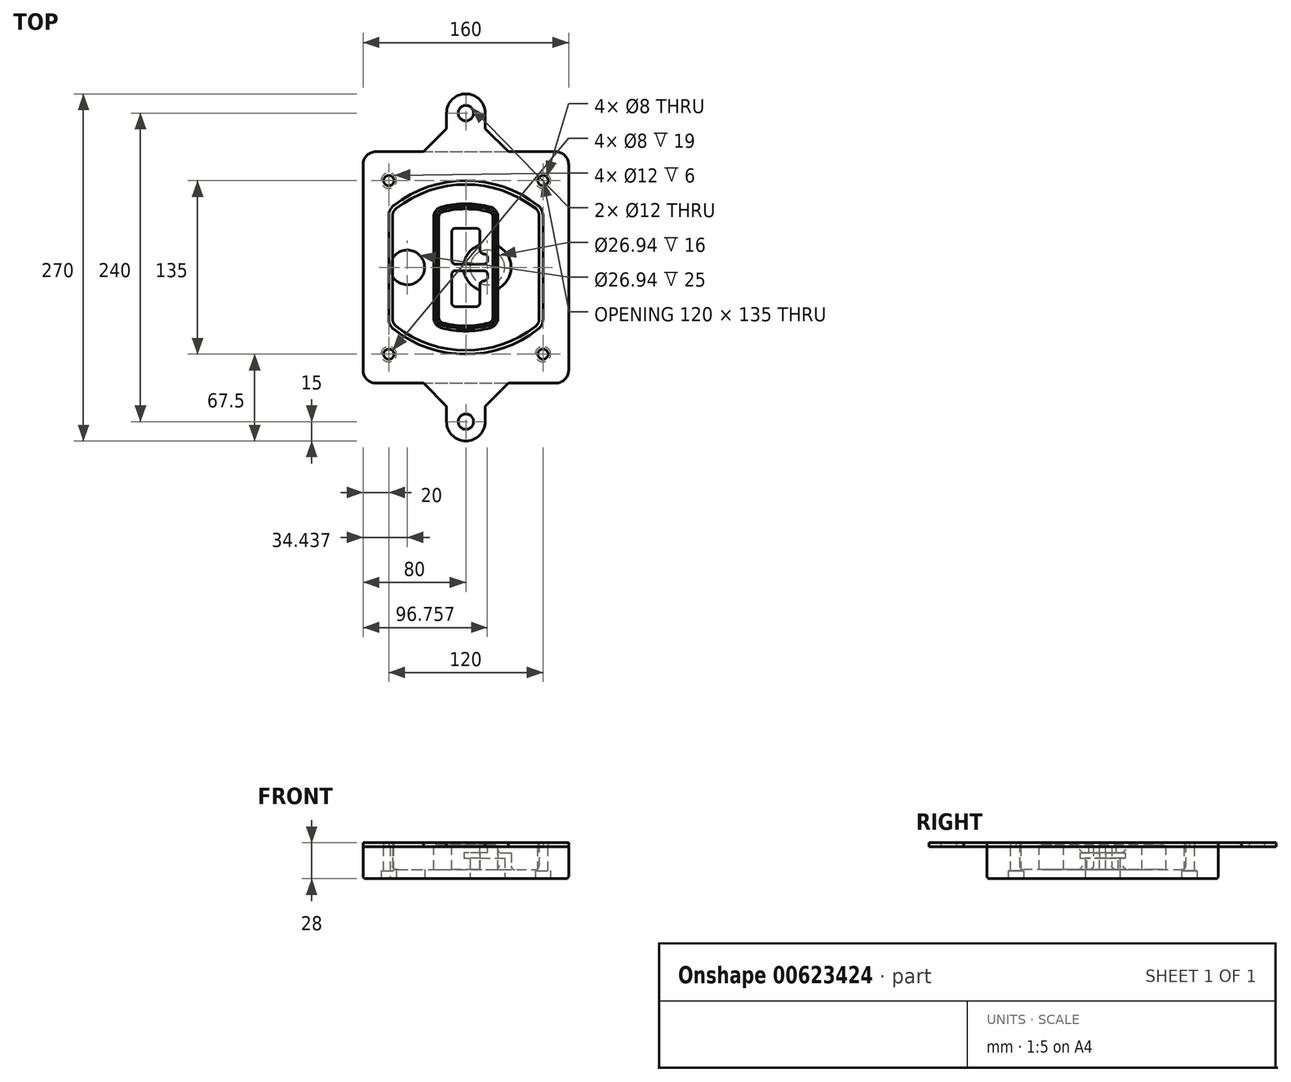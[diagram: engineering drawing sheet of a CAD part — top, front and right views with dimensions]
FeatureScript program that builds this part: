
annotation { "Feature Type Name" : "Feature", "Feature Type Description" : "" }
export const myFeature = defineFeature(function(context is Context, id is Id, definition is map)
    precondition{}
    {
        {
            var Q0;
            Q0=qCreatedBy(makeId("Top.planeOp"),FACE);
            var sketch = newSketch(context, id + "F0", { "sketchPlane" : qUnion([Q0])});
            skPoint(sketch, "E0.rect.middle", {"position": v(0, 0) * mm});
            skLineSegment(sketch, "E1.bottom", {"start": v(-70, -90) * mm, "end": v(70, -90) * mm});
            skLineSegment(sketch, "E1.top", {"start": v(-70, 90) * mm, "end": v(70, 90) * mm});
            skLineSegment(sketch, "E1.left", {"start": v(-80, -80) * mm, "end": v(-80, 80) * mm});
            skLineSegment(sketch, "E1.right", {"start": v(80, -80) * mm, "end": v(80, 80) * mm});
            skLineSegment(sketch, "E2", {"start": v(-80, 90) * mm, "end": v(80, -90) * mm, "construction": true});
            skLineSegment(sketch, "E3", {"start": v(80, 90) * mm, "end": v(-80, -90) * mm, "construction": true});
            skCircle(sketch, "E4", {"center": v(-60, 67.5) * mm, "radius": 4 * mm});
            skCircle(sketch, "E5", {"center": v(60, 67.5) * mm, "radius": 4 * mm});
            skCircle(sketch, "E6", {"center": v(60, -67.5) * mm, "radius": 4 * mm});
            skCircle(sketch, "E7", {"center": v(-60, -67.5) * mm, "radius": 4 * mm});
            skLineSegment(sketch, "E8", {"start": v(-60, 67.5) * mm, "end": v(60, 67.5) * mm, "construction": true});
            skLineSegment(sketch, "E9", {"start": v(60, 67.5) * mm, "end": v(60, -67.5) * mm, "construction": true});
            skLineSegment(sketch, "E10", {"start": v(60, -67.5) * mm, "end": v(-60, -67.5) * mm, "construction": true});
            skLineSegment(sketch, "E11", {"start": v(-60, -67.5) * mm, "end": v(-60, 67.5) * mm, "construction": true});
            skLineSegment(sketch, "E12", {"start": v(-60, 40.3) * mm, "end": v(-60, -40.3) * mm});
            skLineSegment(sketch, "E13", {"start": v(60, 40.3) * mm, "end": v(60, -40.3) * mm});
            skArc(sketch, "E14", {"start": v(56.15, 48.18) * mm, "mid": v(0, 67.5) * mm, "end": v(-56.15, 48.18) * mm});
            skArc(sketch, "E15", {"start": v(-56.15, -48.18) * mm, "mid": v(0, -67.5) * mm, "end": v(56.15, -48.18) * mm});
            skLineSegment(sketch, "E16", {"start": v(-60, 0) * mm, "end": v(60, 0) * mm, "construction": true});
            skPoint(sketch, "E17.visualSharp", {"position": v(-60, -45) * mm});
            skArc(sketch, "E17.filletArc", {"start": v(-60, -40.3) * mm, "mid": v(-58.99, -44.68) * mm, "end": v(-56.15, -48.18) * mm});
            skPoint(sketch, "E18.visualSharp", {"position": v(-60, 45) * mm});
            skArc(sketch, "E18.filletArc", {"start": v(-56.15, 48.18) * mm, "mid": v(-58.99, 44.68) * mm, "end": v(-60, 40.3) * mm});
            skPoint(sketch, "E19.visualSharp", {"position": v(60, 45) * mm});
            skArc(sketch, "E19.filletArc", {"start": v(60, 40.3) * mm, "mid": v(58.99, 44.68) * mm, "end": v(56.15, 48.18) * mm});
            skPoint(sketch, "E20.visualSharp", {"position": v(60, -45) * mm});
            skArc(sketch, "E20.filletArc", {"start": v(56.15, -48.18) * mm, "mid": v(58.99, -44.68) * mm, "end": v(60, -40.3) * mm});
            skPoint(sketch, "E21.visualSharp", {"position": v(-80, 90) * mm});
            skArc(sketch, "E21.filletArc", {"start": v(-70, 90) * mm, "mid": v(-77.07, 87.07) * mm, "end": v(-80, 80) * mm});
            skPoint(sketch, "E22.visualSharp", {"position": v(80, 90) * mm});
            skArc(sketch, "E22.filletArc", {"start": v(80, 80) * mm, "mid": v(77.07, 87.07) * mm, "end": v(70, 90) * mm});
            skPoint(sketch, "E23.visualSharp", {"position": v(80, -90) * mm});
            skArc(sketch, "E23.filletArc", {"start": v(70, -90) * mm, "mid": v(77.07, -87.07) * mm, "end": v(80, -80) * mm});
            skPoint(sketch, "E24.visualSharp", {"position": v(-80, -90) * mm});
            skArc(sketch, "E24.filletArc", {"start": v(-80, -80) * mm, "mid": v(-77.07, -87.07) * mm, "end": v(-70, -90) * mm});
            skArc(sketch, "E25.0", {"start": v(57, 40.3) * mm, "mid": v(56.3, 43.36) * mm, "end": v(54.3, 45.81) * mm});
            skLineSegment(sketch, "E25.1", {"start": v(57, 40.3) * mm, "end": v(57, -40.3) * mm});
            skArc(sketch, "E25.2", {"start": v(54.3, -45.81) * mm, "mid": v(56.3, -43.36) * mm, "end": v(57, -40.3) * mm});
            skArc(sketch, "E25.3", {"start": v(-54.3, -45.81) * mm, "mid": v(0, -64.5) * mm, "end": v(54.3, -45.81) * mm});
            skArc(sketch, "E25.4", {"start": v(-57, -40.3) * mm, "mid": v(-56.3, -43.36) * mm, "end": v(-54.3, -45.81) * mm});
            skArc(sketch, "E25.5", {"start": v(54.3, 45.81) * mm, "mid": v(0, 64.5) * mm, "end": v(-54.3, 45.81) * mm});
            skLineSegment(sketch, "E25.6", {"start": v(-57, 40.3) * mm, "end": v(-57, -40.3) * mm});
            skArc(sketch, "E25.7", {"start": v(-54.3, 45.81) * mm, "mid": v(-56.3, 43.36) * mm, "end": v(-57, 40.3) * mm});
            skArc(sketch, "E26.0", {"start": v(-58.62, 51.33) * mm, "mid": v(-62.58, 46.43) * mm, "end": v(-64, 40.3) * mm});
            skArc(sketch, "E26.1", {"start": v(58.62, 51.33) * mm, "mid": v(0, 71.5) * mm, "end": v(-58.62, 51.33) * mm});
            skArc(sketch, "E26.2", {"start": v(64, 40.3) * mm, "mid": v(62.58, 46.43) * mm, "end": v(58.62, 51.33) * mm});
            skLineSegment(sketch, "E26.3", {"start": v(64, 40.3) * mm, "end": v(64, -40.3) * mm});
            skArc(sketch, "E26.4", {"start": v(58.62, -51.33) * mm, "mid": v(62.58, -46.43) * mm, "end": v(64, -40.3) * mm});
            skLineSegment(sketch, "E26.5", {"start": v(-64, 40.3) * mm, "end": v(-64, -40.3) * mm});
            skArc(sketch, "E26.6", {"start": v(-58.62, -51.33) * mm, "mid": v(0, -71.5) * mm, "end": v(58.62, -51.33) * mm});
            skArc(sketch, "E26.7", {"start": v(-64, -40.3) * mm, "mid": v(-62.58, -46.43) * mm, "end": v(-58.62, -51.33) * mm});
            skSolve(sketch);
        }
        {
            var Q0;
            Q0=makeQuery(id+"F0.imprint","IMPRINT",FACE,{"disambiguationData":[TD([[makeQuery(id+"F0.imprint","IMPRINT",EDGE,{"derivedFrom":sQuery(id+"F0.wireOp",EDGE,"E1.bottom")}),1.0]])]});
            var Q1;
            Q1=makeQuery(id+"F0.imprint","IMPRINT",FACE,{"disambiguationData":[TD([[makeQuery(id+"F0.imprint","IMPRINT",EDGE,{"derivedFrom":sQuery(id+"F0.wireOp",EDGE,"E12")}),1.0]])]});
            var Q2;
            Q2=makeQuery(id+"F0.imprint","IMPRINT",FACE,{"disambiguationData":[TD([[makeQuery(id+"F0.imprint","IMPRINT",EDGE,{"derivedFrom":sQuery(id+"F0.wireOp",EDGE,"E25.0")}),1.0]])]});
            var Q3;
            Q3=makeQuery(id+"F0.imprint","IMPRINT",FACE,{"disambiguationData":[TD([[makeQuery(id+"F0.imprint","IMPRINT",EDGE,{"derivedFrom":sQuery(id+"F0.wireOp",EDGE,"E12")}),-1.0]])]});
            extrude(context, id + "F1", {"entities" : qUnion([Q0, Q1, Q2, Q3]), "oppositeDirection" : true, "depth" : 25 * mm});
        }
        {
            var Q0;
            Q0=makeQuery(id+"F0.imprint","IMPRINT",FACE,{"disambiguationData":[TD([[makeQuery(id+"F0.imprint","IMPRINT",EDGE,{"derivedFrom":sQuery(id+"F0.wireOp",EDGE,"E12")}),1.0]])]});
            extrude(context, id + "F2", {"entities" : qUnion([Q0]), "operationType" : NewBodyOperationType.ADD, "depth" : 3 * mm});
        }
        {
            var Q0;
            Q0=makeQuery(id+"F0.imprint","IMPRINT",FACE,{"disambiguationData":[TD([[makeQuery(id+"F0.imprint","IMPRINT",EDGE,{"derivedFrom":sQuery(id+"F0.wireOp",EDGE,"E25.0")}),1.0]])]});
            extrude(context, id + "F3", {"entities" : qUnion([Q0]), "operationType" : NewBodyOperationType.REMOVE, "oppositeDirection" : true, "depth" : 18 * mm});
        }
        {
            var Q0;
            Q0=makeQuery(id+"F2.opExtrude","CAP_FACE",FACE,{"disambiguationData":[OSD([sQuery(id+"F0.wireOp",EDGE,"E12"),sQuery(id+"F0.wireOp",EDGE,"E13"),sQuery(id+"F0.wireOp",EDGE,"E14"),sQuery(id+"F0.wireOp",EDGE,"E15"),sQuery(id+"F0.wireOp",EDGE,"E17.filletArc"),sQuery(id+"F0.wireOp",EDGE,"E18.filletArc"),sQuery(id+"F0.wireOp",EDGE,"E19.filletArc"),sQuery(id+"F0.wireOp",EDGE,"E20.filletArc"),sQuery(id+"F0.wireOp",EDGE,"E25.0"),sQuery(id+"F0.wireOp",EDGE,"E25.1"),sQuery(id+"F0.wireOp",EDGE,"E25.2"),sQuery(id+"F0.wireOp",EDGE,"E25.3"),sQuery(id+"F0.wireOp",EDGE,"E25.4"),sQuery(id+"F0.wireOp",EDGE,"E25.5"),sQuery(id+"F0.wireOp",EDGE,"E25.6"),sQuery(id+"F0.wireOp",EDGE,"E25.7")])],"isStart":false});
            var sketch = newSketch(context, id + "F4", { "sketchPlane" : qUnion([Q0])});
            skArc(sketch, "E27.0", {"start": v(-19.08, -46.97) * mm, "mid": v(0, -49.5) * mm, "end": v(19.08, -46.97) * mm});
            skArc(sketch, "E28.0", {"start": v(19.08, 46.97) * mm, "mid": v(0, 49.5) * mm, "end": v(-19.08, 46.97) * mm});
            skLineSegment(sketch, "E29", {"start": v(-25, 39.25) * mm, "end": v(-25, -39.25) * mm});
            skLineSegment(sketch, "E30", {"start": v(25, 39.25) * mm, "end": v(25, -39.25) * mm});
            skLineSegment(sketch, "E31", {"start": v(-25, 45.1) * mm, "end": v(25, 45.1) * mm, "construction": true});
            skLineSegment(sketch, "E32", {"start": v(-25, -45.1) * mm, "end": v(25, -45.1) * mm, "construction": true});
            skPoint(sketch, "E33.visualSharp", {"position": v(-25, 45.1) * mm});
            skArc(sketch, "E33.filletArc", {"start": v(-19.08, 46.97) * mm, "mid": v(-23.35, 44.11) * mm, "end": v(-25, 39.25) * mm});
            skPoint(sketch, "E34.visualSharp", {"position": v(25, 45.1) * mm});
            skArc(sketch, "E34.filletArc", {"start": v(25, 39.25) * mm, "mid": v(23.35, 44.11) * mm, "end": v(19.08, 46.97) * mm});
            skPoint(sketch, "E35.visualSharp", {"position": v(25, -45.1) * mm});
            skArc(sketch, "E35.filletArc", {"start": v(19.08, -46.97) * mm, "mid": v(23.35, -44.11) * mm, "end": v(25, -39.25) * mm});
            skPoint(sketch, "E36.visualSharp", {"position": v(-25, -45.1) * mm});
            skArc(sketch, "E36.filletArc", {"start": v(-25, -39.25) * mm, "mid": v(-23.35, -44.11) * mm, "end": v(-19.08, -46.97) * mm});
            skArc(sketch, "E37.0", {"start": v(54.3, 45.81) * mm, "mid": v(0, 64.5) * mm, "end": v(-54.3, 45.81) * mm});
            skArc(sketch, "E37.1", {"start": v(-54.3, 45.81) * mm, "mid": v(-56.3, 43.36) * mm, "end": v(-57, 40.3) * mm});
            skLineSegment(sketch, "E37.2", {"start": v(-57, 40.3) * mm, "end": v(-57, -40.3) * mm});
            skArc(sketch, "E37.3", {"start": v(-57, -40.3) * mm, "mid": v(-56.3, -43.36) * mm, "end": v(-54.3, -45.81) * mm});
            skArc(sketch, "E37.4", {"start": v(-54.3, -45.81) * mm, "mid": v(0, -64.5) * mm, "end": v(54.3, -45.81) * mm});
            skArc(sketch, "E37.5", {"start": v(54.3, -45.81) * mm, "mid": v(56.3, -43.36) * mm, "end": v(57, -40.3) * mm});
            skLineSegment(sketch, "E37.6", {"start": v(57, 40.3) * mm, "end": v(57, -40.3) * mm});
            skArc(sketch, "E37.7", {"start": v(57, 40.3) * mm, "mid": v(56.3, 43.36) * mm, "end": v(54.3, 45.81) * mm});
            skLineSegment(sketch, "E38.0", {"start": v(23, 39.25) * mm, "end": v(23, -39.25) * mm});
            skArc(sketch, "E38.1", {"start": v(18.56, -45.04) * mm, "mid": v(21.76, -42.9) * mm, "end": v(23, -39.25) * mm});
            skArc(sketch, "E38.2", {"start": v(-18.56, -45.04) * mm, "mid": v(0, -47.5) * mm, "end": v(18.56, -45.04) * mm});
            skArc(sketch, "E38.3", {"start": v(-23, -39.25) * mm, "mid": v(-21.76, -42.9) * mm, "end": v(-18.56, -45.04) * mm});
            skLineSegment(sketch, "E38.4", {"start": v(-23, 39.25) * mm, "end": v(-23, -39.25) * mm});
            skArc(sketch, "E38.5", {"start": v(23, 39.25) * mm, "mid": v(21.76, 42.9) * mm, "end": v(18.56, 45.04) * mm});
            skArc(sketch, "E38.6", {"start": v(-18.56, 45.04) * mm, "mid": v(-21.76, 42.9) * mm, "end": v(-23, 39.25) * mm});
            skArc(sketch, "E38.7", {"start": v(18.56, 45.04) * mm, "mid": v(0, 47.5) * mm, "end": v(-18.56, 45.04) * mm});
            skArc(sketch, "E39.0", {"start": v(21, 39.25) * mm, "mid": v(20.18, 41.68) * mm, "end": v(18.04, 43.1) * mm});
            skLineSegment(sketch, "E39.1", {"start": v(21, 39.25) * mm, "end": v(21, -39.25) * mm});
            skArc(sketch, "E39.2", {"start": v(18.04, -43.1) * mm, "mid": v(20.18, -41.68) * mm, "end": v(21, -39.25) * mm});
            skArc(sketch, "E39.3", {"start": v(-18.04, -43.1) * mm, "mid": v(0, -45.5) * mm, "end": v(18.04, -43.1) * mm});
            skArc(sketch, "E39.4", {"start": v(-21, -39.25) * mm, "mid": v(-20.18, -41.68) * mm, "end": v(-18.04, -43.1) * mm});
            skArc(sketch, "E39.5", {"start": v(18.04, 43.1) * mm, "mid": v(0, 45.5) * mm, "end": v(-18.04, 43.1) * mm});
            skLineSegment(sketch, "E39.6", {"start": v(-21, 39.25) * mm, "end": v(-21, -39.25) * mm});
            skArc(sketch, "E39.7", {"start": v(-18.04, 43.1) * mm, "mid": v(-20.18, 41.68) * mm, "end": v(-21, 39.25) * mm});
            skLineSegment(sketch, "E40", {"start": v(-25, 0) * mm, "end": v(25, 0) * mm, "construction": true});
            skLineSegment(sketch, "E41", {"start": v(-11, 5.5) * mm, "end": v(-11, 27.5) * mm});
            skLineSegment(sketch, "E42", {"start": v(-8, 30.5) * mm, "end": v(8, 30.5) * mm});
            skLineSegment(sketch, "E43", {"start": v(11, 27.5) * mm, "end": v(11, 13.5) * mm});
            skLineSegment(sketch, "E44", {"start": v(14, 10.5) * mm, "end": v(14, 10.5) * mm});
            skLineSegment(sketch, "E45", {"start": v(17, 7.5) * mm, "end": v(17, 5.5) * mm});
            skLineSegment(sketch, "E46", {"start": v(14, 2.5) * mm, "end": v(-8, 2.5) * mm});
            skPoint(sketch, "E47.visualSharp", {"position": v(-11, 30.5) * mm});
            skArc(sketch, "E47.filletArc", {"start": v(-8, 30.5) * mm, "mid": v(-10.12, 29.62) * mm, "end": v(-11, 27.5) * mm});
            skPoint(sketch, "E48.visualSharp", {"position": v(11, 30.5) * mm});
            skArc(sketch, "E48.filletArc", {"start": v(11, 27.5) * mm, "mid": v(10.12, 29.62) * mm, "end": v(8, 30.5) * mm});
            skPoint(sketch, "E49.visualSharp", {"position": v(11, 10.5) * mm});
            skArc(sketch, "E49.filletArc", {"start": v(11, 13.5) * mm, "mid": v(11.88, 11.38) * mm, "end": v(14, 10.5) * mm});
            skPoint(sketch, "E50.visualSharp", {"position": v(17, 10.5) * mm});
            skArc(sketch, "E50.filletArc", {"start": v(17, 7.5) * mm, "mid": v(16.12, 9.62) * mm, "end": v(14, 10.5) * mm});
            skPoint(sketch, "E51.visualSharp", {"position": v(17, 2.5) * mm});
            skArc(sketch, "E51.filletArc", {"start": v(14, 2.5) * mm, "mid": v(16.12, 3.38) * mm, "end": v(17, 5.5) * mm});
            skPoint(sketch, "E52.visualSharp", {"position": v(-11, 2.5) * mm});
            skArc(sketch, "E52.filletArc", {"start": v(-11, 5.5) * mm, "mid": v(-10.12, 3.38) * mm, "end": v(-8, 2.5) * mm});
            skLineSegment(sketch, "E53.0.MirrorCS", {"start": v(14, -2.5) * mm, "end": v(-8, -2.5) * mm});
            skArc(sketch, "E54.0.MirrorCS", {"start": v(-11, -5.5) * mm, "mid": v(-10.12, -3.38) * mm, "end": v(-8, -2.5) * mm});
            skLineSegment(sketch, "E55.0.MirrorCS", {"start": v(-11, -5.5) * mm, "end": v(-11, -27.5) * mm});
            skArc(sketch, "E56.0.MirrorCS", {"start": v(-8, -30.5) * mm, "mid": v(-10.12, -29.62) * mm, "end": v(-11, -27.5) * mm});
            skLineSegment(sketch, "E57.0.MirrorCS", {"start": v(-8, -30.5) * mm, "end": v(8, -30.5) * mm});
            skArc(sketch, "E58.0.MirrorCS", {"start": v(11, -27.5) * mm, "mid": v(10.12, -29.62) * mm, "end": v(8, -30.5) * mm});
            skLineSegment(sketch, "E59.0.MirrorCS", {"start": v(11, -27.5) * mm, "end": v(11, -13.5) * mm});
            skArc(sketch, "E60.0.MirrorCS", {"start": v(11, -13.5) * mm, "mid": v(11.88, -11.38) * mm, "end": v(14, -10.5) * mm});
            skArc(sketch, "E61.0.MirrorCS", {"start": v(17, -7.5) * mm, "mid": v(16.12, -9.62) * mm, "end": v(14, -10.5) * mm});
            skLineSegment(sketch, "E62.0.MirrorCS", {"start": v(17, -7.5) * mm, "end": v(17, -5.5) * mm});
            skArc(sketch, "E63.0.MirrorCS", {"start": v(14, -2.5) * mm, "mid": v(16.12, -3.38) * mm, "end": v(17, -5.5) * mm});
            skSolve(sketch);
        }
        {
            var Q0;
            Q0=makeQuery(id+"F4.imprint","IMPRINT",FACE,{"disambiguationData":[TD([[makeQuery(id+"F4.imprint","IMPRINT",EDGE,{"derivedFrom":sQuery(id+"F4.wireOp",EDGE,"E27.0")}),1.0]])]});
            var Q1;
            Q1=makeQuery(id+"F4.imprint","IMPRINT",FACE,{"disambiguationData":[TD([[makeQuery(id+"F4.imprint","IMPRINT",EDGE,{"derivedFrom":sQuery(id+"F4.wireOp",EDGE,"E38.0")}),-1.0]])]});
            var Q2;
            Q2=makeQuery(id+"F4.imprint","IMPRINT",FACE,{"disambiguationData":[TD([[makeQuery(id+"F4.imprint","IMPRINT",EDGE,{"derivedFrom":sQuery(id+"F4.wireOp",EDGE,"E39.0")}),1.0]])]});
            extrude(context, id + "F5", {"entities" : qUnion([Q0, Q1, Q2]), "operationType" : NewBodyOperationType.ADD, "endBound" : BoundingType.UP_TO_NEXT, "oppositeDirection" : true, "depth" : 25 * mm});
        }
        {
            var Q0;
            Q0=makeQuery(id+"F4.imprint","IMPRINT",FACE,{"disambiguationData":[TD([[makeQuery(id+"F4.imprint","IMPRINT",EDGE,{"derivedFrom":sQuery(id+"F4.wireOp",EDGE,"E38.0")}),-1.0]])]});
            extrude(context, id + "F6", {"entities" : qUnion([Q0]), "operationType" : NewBodyOperationType.REMOVE, "oppositeDirection" : true, "depth" : 2 * mm});
        }
        {
            var Q0;
            Q0=makeQuery(id+"F1.opExtrude","CAP_FACE",FACE,{"disambiguationData":[OSD([sQuery(id+"F0.wireOp",EDGE,"E1.bottom"),sQuery(id+"F0.wireOp",EDGE,"E1.top"),sQuery(id+"F0.wireOp",EDGE,"E1.left"),sQuery(id+"F0.wireOp",EDGE,"E1.right"),sQuery(id+"F0.wireOp",EDGE,"E4"),sQuery(id+"F0.wireOp",EDGE,"E5"),sQuery(id+"F0.wireOp",EDGE,"E6"),sQuery(id+"F0.wireOp",EDGE,"E7"),sQuery(id+"F0.wireOp",EDGE,"E21.filletArc"),sQuery(id+"F0.wireOp",EDGE,"E22.filletArc"),sQuery(id+"F0.wireOp",EDGE,"E23.filletArc"),sQuery(id+"F0.wireOp",EDGE,"E24.filletArc")])],"isStart":false});
            var sketch = newSketch(context, id + "F7", { "sketchPlane" : qUnion([Q0])});
            skCircle(sketch, "E64", {"center": v(16.76, 0) * mm, "radius": 13.47 * mm});
            skCircle(sketch, "E65", {"center": v(-45.56, 0) * mm, "radius": 13.47 * mm});
            skLineSegment(sketch, "E66", {"start": v(80, 0) * mm, "end": v(-80, 0) * mm});
            skCircle(sketch, "E67", {"center": v(16.76, 0) * mm, "radius": 18.47 * mm});
            skCircle(sketch, "E68", {"center": v(60, -67.5) * mm, "radius": 6 * mm});
            skCircle(sketch, "E69", {"center": v(-60, -67.5) * mm, "radius": 6 * mm});
            skCircle(sketch, "E70", {"center": v(-60, 67.5) * mm, "radius": 6 * mm});
            skCircle(sketch, "E71", {"center": v(60, 67.5) * mm, "radius": 6 * mm});
            skSolve(sketch);
        }
        {
            var Q0;
            {var subQ1=sQuery(id+"F7.wireOp",EDGE,"E66");var subQ4=sQuery(id+"F7.wireOp",EDGE,"E64");var subQ6=makeQuery(id+"F7.imprint","INTERSECT",VERTEX,{"disambiguationData":[OD(0.0)],"derivedFrom":[subQ4,subQ1]});Q0=makeQuery(id+"F7.imprint","IMPRINT",FACE,{"disambiguationData":[TD([[makeQuery(id+"F7.imprint","IMPRINT",EDGE,{"disambiguationData":[TD([[subQ6,-1.0]])],"derivedFrom":subQ4}),-1.0]])]});}
            var Q1;
            {var subQ0=sQuery(id+"F7.wireOp",EDGE,"E66");var subQ1=sQuery(id+"F7.wireOp",EDGE,"E64");var subQ3=makeQuery(id+"F7.imprint","INTERSECT",VERTEX,{"disambiguationData":[OD(0.0)],"derivedFrom":[subQ1,subQ0]});Q1=makeQuery(id+"F7.imprint","IMPRINT",FACE,{"disambiguationData":[TD([[makeQuery(id+"F7.imprint","IMPRINT",EDGE,{"disambiguationData":[TD([[subQ3,-1.0]])],"derivedFrom":subQ1}),1.0]])]});}
            var Q2;
            {var subQ0=sQuery(id+"F7.wireOp",EDGE,"E66");var subQ1=sQuery(id+"F7.wireOp",EDGE,"E64");var subQ3=makeQuery(id+"F7.imprint","INTERSECT",VERTEX,{"disambiguationData":[OD(0.0)],"derivedFrom":[subQ1,subQ0]});Q2=makeQuery(id+"F7.imprint","IMPRINT",FACE,{"disambiguationData":[TD([[makeQuery(id+"F7.imprint","IMPRINT",EDGE,{"disambiguationData":[TD([[subQ3,1.0]])],"derivedFrom":subQ1}),1.0]])]});}
            var Q3;
            {var subQ1=sQuery(id+"F7.wireOp",EDGE,"E66");var subQ4=sQuery(id+"F7.wireOp",EDGE,"E64");var subQ6=makeQuery(id+"F7.imprint","INTERSECT",VERTEX,{"disambiguationData":[OD(0.0)],"derivedFrom":[subQ4,subQ1]});Q3=makeQuery(id+"F7.imprint","IMPRINT",FACE,{"disambiguationData":[TD([[makeQuery(id+"F7.imprint","IMPRINT",EDGE,{"disambiguationData":[TD([[subQ6,1.0]])],"derivedFrom":subQ4}),-1.0]])]});}
            extrude(context, id + "F8", {"entities" : qUnion([Q0, Q1, Q2, Q3]), "operationType" : NewBodyOperationType.ADD, "oppositeDirection" : true, "depth" : 20 * mm});
        }
        {
            var Q0;
            {var subQ0=sQuery(id+"F7.wireOp",EDGE,"E66");var subQ1=sQuery(id+"F7.wireOp",EDGE,"E64");var subQ3=makeQuery(id+"F7.imprint","INTERSECT",VERTEX,{"disambiguationData":[OD(0.0)],"derivedFrom":[subQ1,subQ0]});Q0=makeQuery(id+"F7.imprint","IMPRINT",FACE,{"disambiguationData":[TD([[makeQuery(id+"F7.imprint","IMPRINT",EDGE,{"disambiguationData":[TD([[subQ3,-1.0]])],"derivedFrom":subQ1}),1.0]])]});}
            var Q1;
            {var subQ0=sQuery(id+"F7.wireOp",EDGE,"E66");var subQ1=sQuery(id+"F7.wireOp",EDGE,"E64");var subQ3=makeQuery(id+"F7.imprint","INTERSECT",VERTEX,{"disambiguationData":[OD(0.0)],"derivedFrom":[subQ1,subQ0]});Q1=makeQuery(id+"F7.imprint","IMPRINT",FACE,{"disambiguationData":[TD([[makeQuery(id+"F7.imprint","IMPRINT",EDGE,{"disambiguationData":[TD([[subQ3,1.0]])],"derivedFrom":subQ1}),1.0]])]});}
            extrude(context, id + "F9", {"entities" : qUnion([Q0, Q1]), "operationType" : NewBodyOperationType.REMOVE, "oppositeDirection" : true, "depth" : 16 * mm});
        }
        {
            var Q0;
            {var subQ0=sQuery(id+"F7.wireOp",EDGE,"E66");var subQ1=sQuery(id+"F7.wireOp",EDGE,"E65");var subQ3=makeQuery(id+"F7.imprint","INTERSECT",VERTEX,{"disambiguationData":[OD(0.0)],"derivedFrom":[subQ1,subQ0]});Q0=makeQuery(id+"F7.imprint","IMPRINT",FACE,{"disambiguationData":[TD([[makeQuery(id+"F7.imprint","IMPRINT",EDGE,{"disambiguationData":[TD([[subQ3,-1.0]])],"derivedFrom":subQ1}),1.0]])]});}
            var Q1;
            {var subQ0=sQuery(id+"F7.wireOp",EDGE,"E66");var subQ1=sQuery(id+"F7.wireOp",EDGE,"E65");var subQ3=makeQuery(id+"F7.imprint","INTERSECT",VERTEX,{"disambiguationData":[OD(0.0)],"derivedFrom":[subQ1,subQ0]});Q1=makeQuery(id+"F7.imprint","IMPRINT",FACE,{"disambiguationData":[TD([[makeQuery(id+"F7.imprint","IMPRINT",EDGE,{"disambiguationData":[TD([[subQ3,1.0]])],"derivedFrom":subQ1}),1.0]])]});}
            extrude(context, id + "F10", {"entities" : qUnion([Q0, Q1]), "operationType" : NewBodyOperationType.REMOVE, "oppositeDirection" : true, "depth" : 25 * mm});
        }
        {
            var Q0;
            Q0=makeQuery(id+"F7.imprint","IMPRINT",FACE,{"disambiguationData":[TD([[makeQuery(id+"F7.imprint","IMPRINT",EDGE,{"derivedFrom":sQuery(id+"F7.wireOp",EDGE,"E68")}),1.0]])]});
            var Q1;
            Q1=makeQuery(id+"F7.imprint","IMPRINT",FACE,{"disambiguationData":[TD([[makeQuery(id+"F7.imprint","IMPRINT",EDGE,{"derivedFrom":makeQuery(id+"F1.opExtrude","CAP_EDGE",EDGE,{"disambiguationData":[OSD([sQuery(id+"F0.wireOp",EDGE,"E5")])],"isStart":false})}),-1.0]])]});
            var Q2;
            Q2=makeQuery(id+"F7.imprint","IMPRINT",FACE,{"disambiguationData":[TD([[makeQuery(id+"F7.imprint","IMPRINT",EDGE,{"derivedFrom":sQuery(id+"F7.wireOp",EDGE,"E69")}),1.0]])]});
            var Q3;
            Q3=makeQuery(id+"F7.imprint","IMPRINT",FACE,{"disambiguationData":[TD([[makeQuery(id+"F7.imprint","IMPRINT",EDGE,{"derivedFrom":makeQuery(id+"F1.opExtrude","CAP_EDGE",EDGE,{"disambiguationData":[OSD([sQuery(id+"F0.wireOp",EDGE,"E4")])],"isStart":false})}),-1.0]])]});
            var Q4;
            Q4=makeQuery(id+"F7.imprint","IMPRINT",FACE,{"disambiguationData":[TD([[makeQuery(id+"F7.imprint","IMPRINT",EDGE,{"derivedFrom":sQuery(id+"F7.wireOp",EDGE,"E70")}),1.0]])]});
            var Q5;
            Q5=makeQuery(id+"F7.imprint","IMPRINT",FACE,{"disambiguationData":[TD([[makeQuery(id+"F7.imprint","IMPRINT",EDGE,{"derivedFrom":makeQuery(id+"F1.opExtrude","CAP_EDGE",EDGE,{"disambiguationData":[OSD([sQuery(id+"F0.wireOp",EDGE,"E7")])],"isStart":false})}),-1.0]])]});
            var Q6;
            Q6=makeQuery(id+"F7.imprint","IMPRINT",FACE,{"disambiguationData":[TD([[makeQuery(id+"F7.imprint","IMPRINT",EDGE,{"derivedFrom":sQuery(id+"F7.wireOp",EDGE,"E71")}),1.0]])]});
            var Q7;
            Q7=makeQuery(id+"F7.imprint","IMPRINT",FACE,{"disambiguationData":[TD([[makeQuery(id+"F7.imprint","IMPRINT",EDGE,{"derivedFrom":makeQuery(id+"F1.opExtrude","CAP_EDGE",EDGE,{"disambiguationData":[OSD([sQuery(id+"F0.wireOp",EDGE,"E6")])],"isStart":false})}),-1.0]])]});
            extrude(context, id + "F11", {"entities" : qUnion([Q0, Q1, Q2, Q3, Q4, Q5, Q6, Q7]), "operationType" : NewBodyOperationType.REMOVE, "oppositeDirection" : true, "depth" : 6 * mm});
        }
        {
            var Q0;
            Q0=makeQuery(id+"F9.boolean.opBoolean","COPY",FACE,{"derivedFrom":makeQuery(id+"F9.opExtrude","CAP_FACE",FACE,{"disambiguationData":[OSD([sQuery(id+"F7.wireOp",EDGE,"E64")])],"isStart":false})});
            var sketch = newSketch(context, id + "F12", { "sketchPlane" : qUnion([Q0])});
            skArc(sketch, "E72.0", {"start": v(11, 17.55) * mm, "mid": v(2.57, 11.82) * mm, "end": v(-1.54, 2.5) * mm});
            skArc(sketch, "E72.1", {"start": v(-1.54, -2.5) * mm, "mid": v(2.57, -11.82) * mm, "end": v(11, -17.55) * mm});
            skLineSegment(sketch, "E73", {"start": v(-1.54, -2.5) * mm, "end": v(14, -2.5) * mm});
            skLineSegment(sketch, "E74.0", {"start": v(14, 2.5) * mm, "end": v(-1.54, 2.5) * mm});
            skArc(sketch, "E74.1", {"start": v(14, 2.5) * mm, "mid": v(16.12, 3.38) * mm, "end": v(17, 5.5) * mm});
            skLineSegment(sketch, "E74.2", {"start": v(17, 7.5) * mm, "end": v(17, 5.5) * mm});
            skArc(sketch, "E74.3", {"start": v(17, 7.5) * mm, "mid": v(16.12, 9.62) * mm, "end": v(14, 10.5) * mm});
            skArc(sketch, "E74.4", {"start": v(11, 13.5) * mm, "mid": v(11.88, 11.38) * mm, "end": v(14, 10.5) * mm});
            skLineSegment(sketch, "E74.5", {"start": v(11, 17.55) * mm, "end": v(11, 13.5) * mm});
            skLineSegment(sketch, "E74.7", {"start": v(14, -2.5) * mm, "end": v(-1.54, -2.5) * mm});
            skArc(sketch, "E74.8", {"start": v(14, -2.5) * mm, "mid": v(16.12, -3.38) * mm, "end": v(17, -5.5) * mm});
            skLineSegment(sketch, "E74.9", {"start": v(17, -7.5) * mm, "end": v(17, -5.5) * mm});
            skArc(sketch, "E74.10", {"start": v(17, -7.5) * mm, "mid": v(16.12, -9.62) * mm, "end": v(14, -10.5) * mm});
            skArc(sketch, "E74.11", {"start": v(11, -13.5) * mm, "mid": v(11.88, -11.38) * mm, "end": v(14, -10.5) * mm});
            skLineSegment(sketch, "E74.12", {"start": v(11, -17.55) * mm, "end": v(11, -13.5) * mm});
            skPoint(sketch, "E75.orphan", {"position": v(11, -27.5) * mm});
            skPoint(sketch, "E76.orphan", {"position": v(-8, -2.5) * mm});
            skPoint(sketch, "E77.orphan", {"position": v(-8, 2.5) * mm});
            skPoint(sketch, "E78.orphan", {"position": v(11, 27.5) * mm});
            skSolve(sketch);
        }
        {
            var Q0;
            {var subQ7=sQuery(id+"F12.wireOp",EDGE,"E72.0");var subQ14=sQuery(id+"F12.wireOp",EDGE,"E72.1");var subQ16=sQuery(id+"F12.wireOp",EDGE,"E74.1");var subQ18=sQuery(id+"F12.wireOp",EDGE,"E74.8");Q0=qUnion([makeQuery(id+"F12.imprint","IMPRINT",FACE,{"disambiguationData":[TD([[makeQuery(id+"F12.imprint","IMPRINT",EDGE,{"derivedFrom":subQ7}),1.0]])]}),makeQuery(id+"F12.imprint","IMPRINT",FACE,{"disambiguationData":[TD([[makeQuery(id+"F12.imprint","IMPRINT",EDGE,{"derivedFrom":subQ14}),1.0]])]}),makeQuery(id+"F12.imprint","IMPRINT",FACE,{"disambiguationData":[TD([[makeQuery(id+"F12.imprint","IMPRINT",EDGE,{"derivedFrom":subQ16}),1.0]])]}),makeQuery(id+"F12.imprint","IMPRINT",FACE,{"disambiguationData":[TD([[makeQuery(id+"F12.imprint","IMPRINT",EDGE,{"derivedFrom":subQ18}),-1.0]])]})]);}
            var Q1;
            Q1=makeQuery(id+"F5.boolean.opBoolean","SPLIT",FACE,{"disambiguationData":[TD([makeQuery(id+"F5.opExtrude","SWEPT_FACE",FACE,{"disambiguationData":[OSD([sQuery(id+"F4.wireOp",EDGE,"E41")])]})])],"derivedFrom":makeQuery(id+"F3.boolean.opBoolean","COPY",FACE,{"derivedFrom":makeQuery(id+"F3.opExtrude","CAP_FACE",FACE,{"disambiguationData":[OSD([sQuery(id+"F0.wireOp",EDGE,"E25.0"),sQuery(id+"F0.wireOp",EDGE,"E25.1"),sQuery(id+"F0.wireOp",EDGE,"E25.2"),sQuery(id+"F0.wireOp",EDGE,"E25.3"),sQuery(id+"F0.wireOp",EDGE,"E25.4"),sQuery(id+"F0.wireOp",EDGE,"E25.5"),sQuery(id+"F0.wireOp",EDGE,"E25.6"),sQuery(id+"F0.wireOp",EDGE,"E25.7")])],"isStart":false})})});
            extrude(context, id + "F13", {"entities" : qUnion([Q0]), "operationType" : NewBodyOperationType.REMOVE, "endBound" : BoundingType.UP_TO_SURFACE, "endBoundEntityFace" : qUnion([Q1]), "depth" : 25 * mm});
        }
        {
            var Q0;
            Q0=makeQuery(id+"F3.boolean.opBoolean","COPY",EDGE,{"derivedFrom":makeQuery(id+"F3.opExtrude","CAP_EDGE",EDGE,{"disambiguationData":[OSD([sQuery(id+"F0.wireOp",EDGE,"E25.6")])],"isStart":false})});
            var Q1;
            Q1=makeQuery(id+"F8.boolean.opBoolean","INTERSECT",EDGE,{"derivedFrom":[makeQuery(id+"F5.opExtrude","SWEPT_FACE",FACE,{"disambiguationData":[OSD([sQuery(id+"F4.wireOp",EDGE,"E30")])]}),makeQuery(id+"F8.opExtrude","CAP_FACE",FACE,{"disambiguationData":[OSD([sQuery(id+"F7.wireOp",EDGE,"E67")])],"isStart":false})]});
            var Q2;
            Q2=makeQuery(id+"F8.boolean.opBoolean","INTERSECT",EDGE,{"disambiguationData":[OD(1.0)],"derivedFrom":[makeQuery(id+"F5.opExtrude","SWEPT_FACE",FACE,{"disambiguationData":[OSD([sQuery(id+"F4.wireOp",EDGE,"E30")])]}),makeQuery(id+"F8.opExtrude","SWEPT_FACE",FACE,{"disambiguationData":[OSD([sQuery(id+"F7.wireOp",EDGE,"E67")])]})]});
            var Q3;
            {var subQ0=sQuery(id+"F4.wireOp",EDGE,"E30");Q3=makeQuery(id+"F8.boolean.opBoolean","SPLIT",EDGE,{"disambiguationData":[TD([makeQuery(id+"F5.opExtrude","SWEPT_FACE",FACE,{"disambiguationData":[OSD([sQuery(id+"F4.wireOp",EDGE,"E35.filletArc")])]})])],"derivedFrom":makeQuery(id+"F5.opExtrude","CAP_EDGE",EDGE,{"disambiguationData":[OSD([subQ0])],"isStart":false})});}
            var Q4;
            {var subQ0=sQuery(id+"F0.wireOp",EDGE,"E25.7");var subQ1=sQuery(id+"F0.wireOp",EDGE,"E25.1");var subQ2=sQuery(id+"F0.wireOp",EDGE,"E25.6");var subQ3=sQuery(id+"F0.wireOp",EDGE,"E25.5");var subQ4=sQuery(id+"F0.wireOp",EDGE,"E25.4");var subQ5=sQuery(id+"F0.wireOp",EDGE,"E25.0");var subQ6=sQuery(id+"F0.wireOp",EDGE,"E25.2");var subQ7=sQuery(id+"F0.wireOp",EDGE,"E25.3");Q4=makeQuery(id+"F8.boolean.opBoolean","INTERSECT",EDGE,{"derivedFrom":[makeQuery(id+"F5.boolean.opBoolean","SPLIT",FACE,{"disambiguationData":[TD([makeQuery(id+"F2.opExtrude","SWEPT_FACE",FACE,{"disambiguationData":[OSD([subQ5])]})])],"derivedFrom":makeQuery(id+"F3.boolean.opBoolean","COPY",FACE,{"derivedFrom":makeQuery(id+"F3.opExtrude","CAP_FACE",FACE,{"disambiguationData":[OSD([subQ5,subQ1,subQ6,subQ7,subQ4,subQ3,subQ2,subQ0])],"isStart":false})})}),makeQuery(id+"F8.opExtrude","SWEPT_FACE",FACE,{"disambiguationData":[OSD([sQuery(id+"F7.wireOp",EDGE,"E67")])]})]});}
            var Q5;
            Q5=makeQuery(id+"F8.boolean.opBoolean","INTERSECT",EDGE,{"disambiguationData":[OD(0.0)],"derivedFrom":[makeQuery(id+"F5.opExtrude","SWEPT_FACE",FACE,{"disambiguationData":[OSD([sQuery(id+"F4.wireOp",EDGE,"E30")])]}),makeQuery(id+"F8.opExtrude","SWEPT_FACE",FACE,{"disambiguationData":[OSD([sQuery(id+"F7.wireOp",EDGE,"E67")])]})]});
            fillet(context, id + "F14", {"entities" : qUnion([Q0, Q1, Q2, Q3, Q4, Q5]), "radius" : 3 * mm, "tangentPropagation" : true, "allowEdgeOverflow" : false});
        }
        {
            var Q0;
            Q0=makeQuery(id+"F1.opExtrude","CAP_EDGE",EDGE,{"disambiguationData":[OSD([sQuery(id+"F0.wireOp",EDGE,"E1.bottom")])],"isStart":false});
            fillet(context, id + "F15", {"entities" : qUnion([Q0]), "radius" : 2 * mm, "tangentPropagation" : true, "allowEdgeOverflow" : false});
        }
        {
            var Q0;
            {var subQ0=sQuery(id+"F0.wireOp",EDGE,"E21.filletArc");var subQ1=sQuery(id+"F0.wireOp",EDGE,"E7");var subQ2=sQuery(id+"F0.wireOp",EDGE,"E6");var subQ3=sQuery(id+"F0.wireOp",EDGE,"E5");var subQ4=sQuery(id+"F0.wireOp",EDGE,"E4");var subQ5=sQuery(id+"F0.wireOp",EDGE,"E22.filletArc");var subQ6=sQuery(id+"F0.wireOp",EDGE,"E1.bottom");var subQ7=sQuery(id+"F0.wireOp",EDGE,"E1.right");var subQ8=sQuery(id+"F0.wireOp",EDGE,"E1.top");var subQ9=sQuery(id+"F0.wireOp",EDGE,"E1.left");var subQ10=sQuery(id+"F0.wireOp",EDGE,"E23.filletArc");var subQ11=sQuery(id+"F0.wireOp",EDGE,"E24.filletArc");Q0=makeQuery(id+"F2.boolean.opBoolean","SPLIT",FACE,{"disambiguationData":[TD([makeQuery(id+"F1.opExtrude","SWEPT_FACE",FACE,{"disambiguationData":[OSD([subQ6])]})])],"derivedFrom":makeQuery(id+"F1.opExtrude","CAP_FACE",FACE,{"disambiguationData":[OSD([subQ6,subQ8,subQ9,subQ7,subQ4,subQ3,subQ2,subQ1,subQ0,subQ5,subQ10,subQ11])],"isStart":true})});}
            var sketch = newSketch(context, id + "F16", { "sketchPlane" : qUnion([Q0])});
            skLineSegment(sketch, "E79.0", {"start": v(-70, 90) * mm, "end": v(70, 90) * mm});
            skArc(sketch, "E79.1", {"start": v(-70, 90) * mm, "mid": v(-77.07, 87.07) * mm, "end": v(-80, 80) * mm});
            skLineSegment(sketch, "E79.2", {"start": v(-80, -80) * mm, "end": v(-80, 80) * mm});
            skArc(sketch, "E79.3", {"start": v(-80, -80) * mm, "mid": v(-77.07, -87.07) * mm, "end": v(-70, -90) * mm});
            skLineSegment(sketch, "E79.4", {"start": v(-70, -90) * mm, "end": v(70, -90) * mm});
            skArc(sketch, "E79.5", {"start": v(70, -90) * mm, "mid": v(77.07, -87.07) * mm, "end": v(80, -80) * mm});
            skLineSegment(sketch, "E79.6", {"start": v(80, -80) * mm, "end": v(80, 80) * mm});
            skArc(sketch, "E79.7", {"start": v(80, 80) * mm, "mid": v(77.07, 87.07) * mm, "end": v(70, 90) * mm});
            skCircle(sketch, "E79.8", {"center": v(-60, 67.5) * mm, "radius": 4 * mm});
            skCircle(sketch, "E79.9", {"center": v(-60, -67.5) * mm, "radius": 4 * mm});
            skCircle(sketch, "E79.10", {"center": v(60, -67.5) * mm, "radius": 4 * mm});
            skCircle(sketch, "E79.11", {"center": v(60, 67.5) * mm, "radius": 4 * mm});
            skLineSegment(sketch, "E79.12", {"start": v(-60, 40.3) * mm, "end": v(-60, -40.3) * mm});
            skArc(sketch, "E79.13", {"start": v(-60, -40.3) * mm, "mid": v(-58.99, -44.68) * mm, "end": v(-56.15, -48.18) * mm});
            skArc(sketch, "E79.14", {"start": v(-56.15, -48.18) * mm, "mid": v(0, -67.5) * mm, "end": v(56.15, -48.18) * mm});
            skArc(sketch, "E79.15", {"start": v(56.15, -48.18) * mm, "mid": v(58.99, -44.68) * mm, "end": v(60, -40.3) * mm});
            skLineSegment(sketch, "E79.16", {"start": v(60, 40.3) * mm, "end": v(60, -40.3) * mm});
            skArc(sketch, "E79.17", {"start": v(60, 40.3) * mm, "mid": v(58.99, 44.68) * mm, "end": v(56.15, 48.18) * mm});
            skArc(sketch, "E79.18", {"start": v(56.15, 48.18) * mm, "mid": v(0, 67.5) * mm, "end": v(-56.15, 48.18) * mm});
            skArc(sketch, "E79.19", {"start": v(-56.15, 48.18) * mm, "mid": v(-58.99, 44.68) * mm, "end": v(-60, 40.3) * mm});
            skLineSegment(sketch, "E80", {"start": v(0, 90) * mm, "end": v(0, 120) * mm, "construction": true});
            skPoint(sketch, "E80.endSnap0", {"position": v(0, 90) * mm});
            skCircle(sketch, "E81", {"center": v(0, 120) * mm, "radius": 6 * mm});
            skArc(sketch, "E82", {"start": v(15, 120) * mm, "mid": v(0, 135) * mm, "end": v(-15, 120) * mm});
            skLineSegment(sketch, "E83", {"start": v(-15, 120) * mm, "end": v(-15, 108) * mm});
            skLineSegment(sketch, "E84", {"start": v(-15, 108) * mm, "end": v(-33, 90) * mm});
            skLineSegment(sketch, "E85.MirrorCS", {"start": v(15, 120) * mm, "end": v(15, 108) * mm});
            skLineSegment(sketch, "E86.MirrorCS", {"start": v(15, 108) * mm, "end": v(33, 90) * mm});
            skLineSegment(sketch, "E87", {"start": v(-80, 0) * mm, "end": v(80, 0) * mm, "construction": true});
            skLineSegment(sketch, "E88.MirrorCS", {"start": v(15, -108) * mm, "end": v(33, -90) * mm});
            skLineSegment(sketch, "E89.MirrorCS", {"start": v(-15, -108) * mm, "end": v(-33, -90) * mm});
            skLineSegment(sketch, "E90.MirrorCS", {"start": v(15, -120) * mm, "end": v(15, -108) * mm});
            skCircle(sketch, "E91.MirrorC", {"center": v(0, -120) * mm, "radius": 6 * mm});
            skLineSegment(sketch, "E92.MirrorCS", {"start": v(-15, -120) * mm, "end": v(-15, -108) * mm});
            skArc(sketch, "E93.MirrorCS", {"start": v(15, -120) * mm, "mid": v(0, -135) * mm, "end": v(-15, -120) * mm});
            skLineSegment(sketch, "E94.MirrorCS", {"start": v(0, -90) * mm, "end": v(0, -120) * mm, "construction": true});
            skSolve(sketch);
        }
        {
            var Q0;
            Q0=makeQuery(id+"F16.imprint","IMPRINT",FACE,{"disambiguationData":[TD([[makeQuery(id+"F16.imprint","IMPRINT",EDGE,{"derivedFrom":sQuery(id+"F16.wireOp",EDGE,"E81")}),-1.0]])]});
            var Q1;
            {var subQ1=sQuery(id+"F16.wireOp",EDGE,"E79.1");Q1=makeQuery(id+"F16.imprint","IMPRINT",FACE,{"disambiguationData":[TD([[makeQuery(id+"F16.imprint","IMPRINT",EDGE,{"derivedFrom":subQ1}),1.0]])]});}
            var Q2;
            {var subQ1=sQuery(id+"F16.wireOp",EDGE,"E88.MirrorCS");Q2=makeQuery(id+"F16.imprint","IMPRINT",FACE,{"disambiguationData":[TD([[makeQuery(id+"F16.imprint","IMPRINT",EDGE,{"derivedFrom":subQ1}),1.0]])]});}
            var Q3;
            Q3=makeQuery(id+"F2.opExtrude","CAP_FACE",FACE,{"disambiguationData":[OSD([sQuery(id+"F0.wireOp",EDGE,"E12"),sQuery(id+"F0.wireOp",EDGE,"E13"),sQuery(id+"F0.wireOp",EDGE,"E14"),sQuery(id+"F0.wireOp",EDGE,"E15"),sQuery(id+"F0.wireOp",EDGE,"E17.filletArc"),sQuery(id+"F0.wireOp",EDGE,"E18.filletArc"),sQuery(id+"F0.wireOp",EDGE,"E19.filletArc"),sQuery(id+"F0.wireOp",EDGE,"E20.filletArc"),sQuery(id+"F0.wireOp",EDGE,"E25.0"),sQuery(id+"F0.wireOp",EDGE,"E25.1"),sQuery(id+"F0.wireOp",EDGE,"E25.2"),sQuery(id+"F0.wireOp",EDGE,"E25.3"),sQuery(id+"F0.wireOp",EDGE,"E25.4"),sQuery(id+"F0.wireOp",EDGE,"E25.5"),sQuery(id+"F0.wireOp",EDGE,"E25.6"),sQuery(id+"F0.wireOp",EDGE,"E25.7")])],"isStart":false});
            extrude(context, id + "F17", {"entities" : qUnion([Q0, Q1, Q2]), "endBound" : BoundingType.UP_TO_SURFACE, "depth" : 25 * mm, "endBoundEntityFace" : qUnion([Q3]), "offsetDistance" : 25 * mm});
        }
    });
